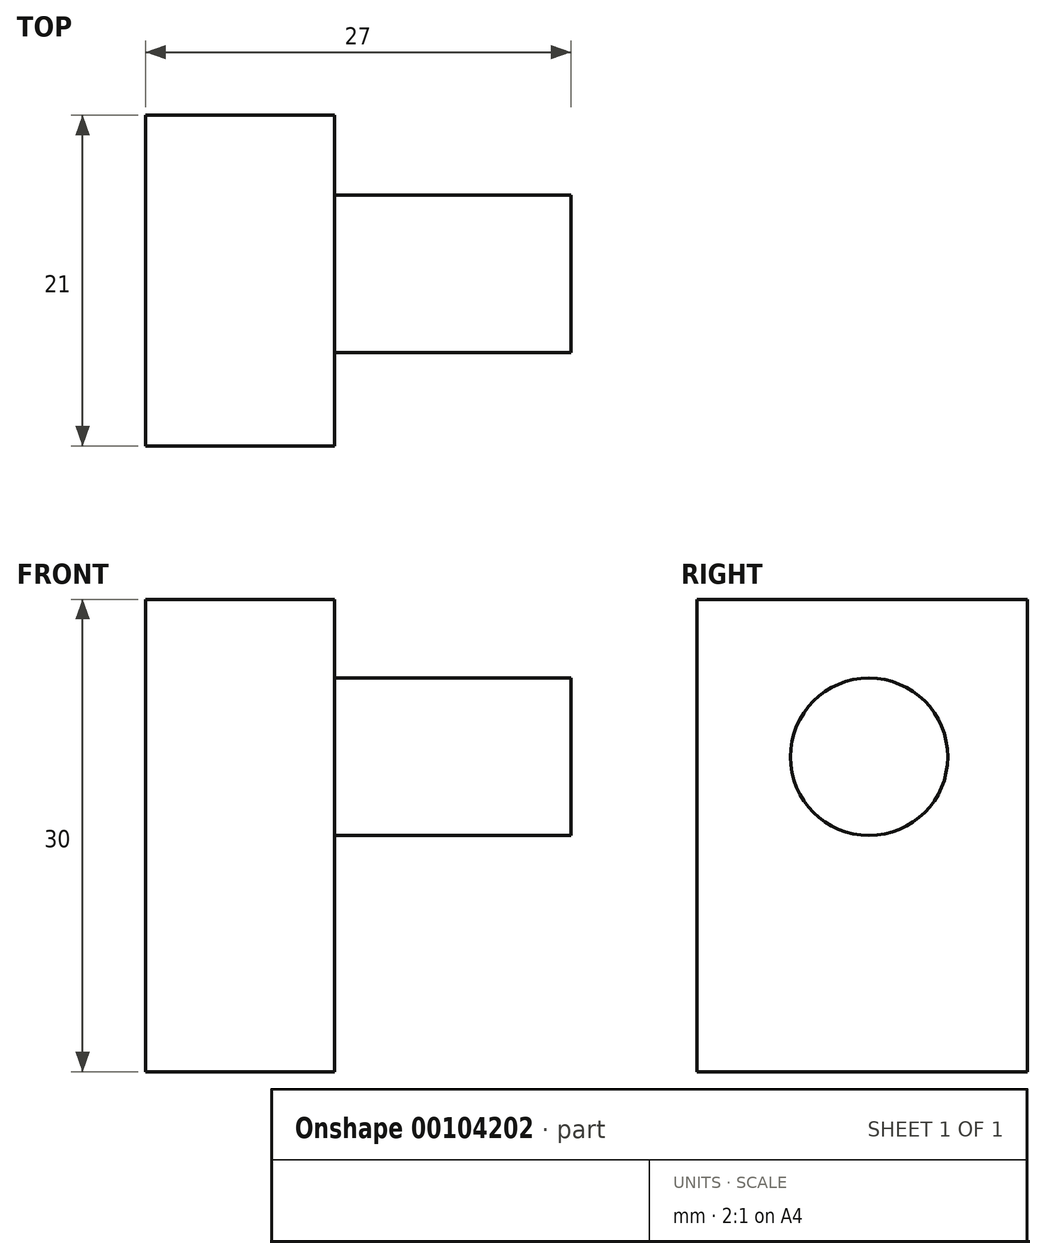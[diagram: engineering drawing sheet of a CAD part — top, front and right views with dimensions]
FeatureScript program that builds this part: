
annotation { "Feature Type Name" : "Feature", "Feature Type Description" : "" }
export const myFeature = defineFeature(function(context is Context, id is Id, definition is map)
    precondition{}
    {
        {
            var Q0;
            Q0=qCreatedBy(makeId("Top.planeOp"),FACE);
            var sketch = newSketch(context, id + "F0", { "sketchPlane" : qUnion([Q0])});
            skLineSegment(sketch, "E0.bottom", {"start": v(-29, 10.06) * mm, "end": v(-17, 10.06) * mm});
            skLineSegment(sketch, "E0.top", {"start": v(-29, -10.94) * mm, "end": v(-17, -10.94) * mm});
            skLineSegment(sketch, "E0.left", {"start": v(-29, 10.06) * mm, "end": v(-29, -10.94) * mm});
            skLineSegment(sketch, "E0.right", {"start": v(-17, 10.06) * mm, "end": v(-17, -10.94) * mm});
            skSolve(sketch);
        }
        {
            var Q0;
            Q0=makeQuery(id+"F0.imprint","IMPRINT",FACE,{"disambiguationData":[TD([[makeQuery(id+"F0.imprint","IMPRINT",EDGE,{"derivedFrom":sQuery(id+"F0.wireOp",EDGE,"E0.bottom")}),-1.0]])]});
            extrude(context, id + "F1", {"entities" : qUnion([Q0]), "depth" : 30 * mm});
        }
        {
            var Q0;
            Q0=makeQuery(id+"F1.opExtrude","SWEPT_FACE",FACE,{"disambiguationData":[OSD([sQuery(id+"F0.wireOp",EDGE,"E0.right")])]});
            var sketch = newSketch(context, id + "F2", { "sketchPlane" : qUnion([Q0])});
            skCircle(sketch, "E1", {"center": v(0, 20) * mm, "radius": 5 * mm});
            skSolve(sketch);
        }
        {
            var Q0;
            Q0=makeQuery(id+"F2.imprint","IMPRINT",FACE,{"disambiguationData":[TD([[makeQuery(id+"F2.imprint","IMPRINT",EDGE,{"derivedFrom":sQuery(id+"F2.wireOp",EDGE,"E1")}),1.0]])]});
            extrude(context, id + "F3", {"entities" : qUnion([Q0]), "operationType" : NewBodyOperationType.ADD, "depth" : 15 * mm});
        }
    });
